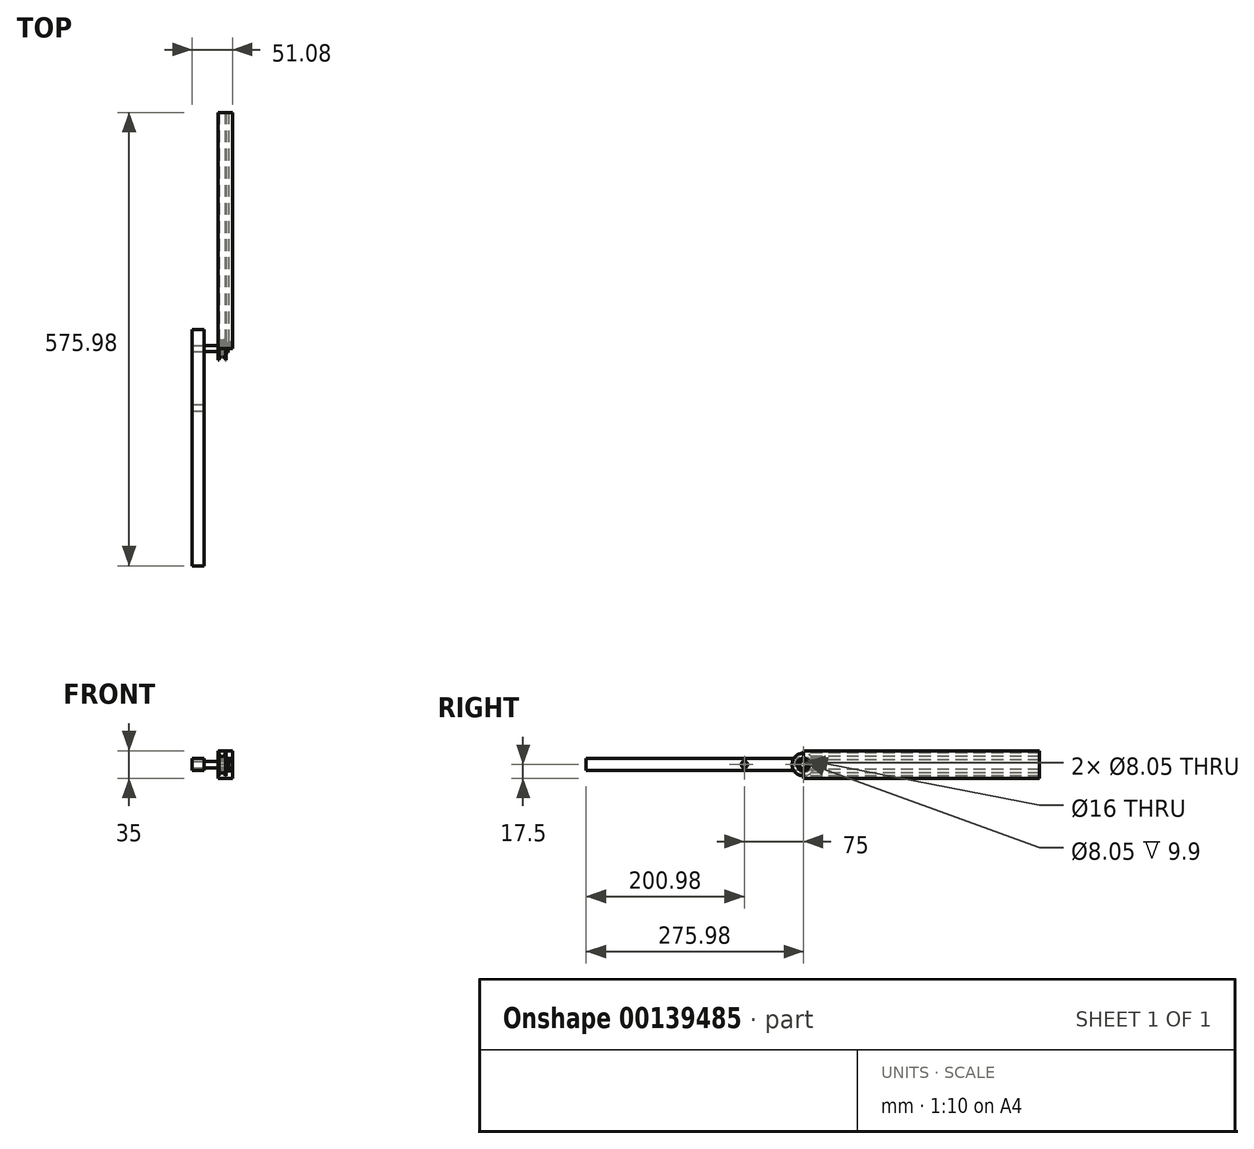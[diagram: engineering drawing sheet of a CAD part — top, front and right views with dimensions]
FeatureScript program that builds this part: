
annotation { "Feature Type Name" : "Feature", "Feature Type Description" : "" }
export const myFeature = defineFeature(function(context is Context, id is Id, definition is map)
    precondition{}
    {
        {
            var Q0;
            Q0=qCreatedBy(makeId("Front.planeOp"),FACE);
            var sketch = newSketch(context, id + "F0", { "sketchPlane" : qUnion([Q0])});
            skLineSegment(sketch, "E0.top", {"start": v(0, 35) * mm, "end": v(-13, 35) * mm});
            skLineSegment(sketch, "E1.0", {"start": v(-3, 32) * mm, "end": v(-13, 32) * mm});
            skLineSegment(sketch, "E1.1", {"start": v(-3, 23.5) * mm, "end": v(-3, 32) * mm});
            skLineSegment(sketch, "E2.trimOffspring", {"start": v(-13, 32) * mm, "end": v(-13, 35) * mm});
            skPoint(sketch, "E3", {"position": v(-4, 32) * mm});
            skPoint(sketch, "E4", {"position": v(-12, 32) * mm});
            skArc(sketch, "E5", {"start": v(-12, 32) * mm, "mid": v(-8, 28) * mm, "end": v(-4, 32) * mm});
            skPoint(sketch, "E0.bottom.start.orphan", {"position": v(0, 0) * mm});
            skPoint(sketch, "E6.MirrorP", {"position": v(-4, 3) * mm});
            skLineSegment(sketch, "E7.MirrorCS", {"start": v(0, 0) * mm, "end": v(-13, 0) * mm});
            skLineSegment(sketch, "E8.MirrorCS", {"start": v(-3, 3) * mm, "end": v(-13, 3) * mm});
            skLineSegment(sketch, "E9.MirrorCS", {"start": v(-3, 11.5) * mm, "end": v(-3, 3) * mm});
            skPoint(sketch, "E10.MirrorP", {"position": v(-12, 3) * mm});
            skArc(sketch, "E11.MirrorCS", {"start": v(-12, 3) * mm, "mid": v(-8, 7) * mm, "end": v(-4, 3) * mm});
            skLineSegment(sketch, "E12.MirrorCS", {"start": v(-13, 3) * mm, "end": v(-13, 0) * mm});
            skLineSegment(sketch, "E13", {"start": v(0, 35) * mm, "end": v(5, 35) * mm});
            skLineSegment(sketch, "E14", {"start": v(5, 35) * mm, "end": v(5, 0) * mm});
            skLineSegment(sketch, "E15", {"start": v(5, 0) * mm, "end": v(0, 0) * mm});
            skLineSegment(sketch, "E16", {"start": v(-3, 23.5) * mm, "end": v(0, 23.5) * mm});
            skLineSegment(sketch, "E17", {"start": v(0, 23.5) * mm, "end": v(0, 17.5) * mm});
            skLineSegment(sketch, "E18", {"start": v(0, 17.5) * mm, "end": v(5, 17.5) * mm, "construction": true});
            skLineSegment(sketch, "E19", {"start": v(0, 17.5) * mm, "end": v(0, 11.5) * mm});
            skLineSegment(sketch, "E20", {"start": v(0, 11.5) * mm, "end": v(-3, 11.5) * mm});
            skSolve(sketch);
        }
        {
            var Q0;
            Q0 = qSketchRegion(id + "F0", true);
            extrude(context, id + "F1", {"entities" : qUnion([Q0]), "oppositeDirection" : true, "depth" : 300 * mm});
        }
        {
            var Q0;
            Q0=qCreatedBy(makeId("Front.planeOp"),FACE);
            var sketch = newSketch(context, id + "F2", { "sketchPlane" : qUnion([Q0])});
            skArc(sketch, "E21.0", {"start": v(-12, 32) * mm, "mid": v(-8, 28) * mm, "end": v(-4, 32) * mm});
            skPoint(sketch, "E21.1", {"position": v(-13, 32) * mm});
            skLineSegment(sketch, "E21.2", {"start": v(-3, 32) * mm, "end": v(-4, 32) * mm});
            skLineSegment(sketch, "E21.3", {"start": v(-3, 23.5) * mm, "end": v(-3, 32) * mm});
            skLineSegment(sketch, "E21.4", {"start": v(-12, 3) * mm, "end": v(-13, 3) * mm});
            skArc(sketch, "E21.5", {"start": v(-12, 3) * mm, "mid": v(-8, 7) * mm, "end": v(-4, 3) * mm});
            skLineSegment(sketch, "E21.6", {"start": v(-3, 3) * mm, "end": v(-4, 3) * mm});
            skLineSegment(sketch, "E22.0", {"start": v(-12, 32) * mm, "end": v(-13, 32) * mm});
            skLineSegment(sketch, "E23.3", {"start": v(-12.1, 31.9) * mm, "end": v(-13, 31.9) * mm});
            skArc(sketch, "E23.4", {"start": v(-12.1, 31.9) * mm, "mid": v(-8, 27.9) * mm, "end": v(-3.9, 31.9) * mm});
            skLineSegment(sketch, "E23.5", {"start": v(-3.1, 31.9) * mm, "end": v(-3.9, 31.9) * mm});
            skLineSegment(sketch, "E23.6", {"start": v(-3.1, 17.5) * mm, "end": v(-3.1, 31.9) * mm});
            skLineSegment(sketch, "E24", {"start": v(-13, 31.9) * mm, "end": v(-13, 17.5) * mm});
            skLineSegment(sketch, "E25", {"start": v(-13, 17.5) * mm, "end": v(-3.1, 17.5) * mm});
            skSolve(sketch);
        }
        {
            var Q0;
            Q0 = qSketchRegion(id + "F2", true);
            var Q1;
            Q1=makeQuery(id+"F2.imprint","IMPRINT",FACE,{"disambiguationData":[TD([[makeQuery(id+"F2.imprint","IMPRINT",EDGE,{"derivedFrom":sQuery(id+"F2.wireOp",EDGE,"E23.3")}),1.0]])]});
            var Q2;
            Q2=sQuery(id+"F2.wireOp",EDGE,"E25");
            revolve(context, id + "F3", {"entities" : qUnion([Q0, Q1]), "axis" : qUnion([Q2]), "revolveType" : RevolveType.FULL});
        }
        {
            var Q0;
            Q0=makeQuery(id+"F3.opRevolve","SWEPT_FACE",FACE,{"disambiguationData":[OSD([sQuery(id+"F2.wireOp",EDGE,"E24")])]});
            var sketch = newSketch(context, id + "F4", { "sketchPlane" : qUnion([Q0])});
            skLineSegment(sketch, "E26", {"start": v(0, 3.1) * mm, "end": v(0, 31.9) * mm, "construction": true});
            skCircle(sketch, "E27", {"center": v(0, 17.5) * mm, "radius": 8 * mm});
            skCircle(sketch, "E28", {"center": v(0, 17.5) * mm, "radius": 4.03 * mm});
            skCircle(sketch, "E29", {"center": v(0, 17.5) * mm, "radius": 5 * mm});
            skCircle(sketch, "E30", {"center": v(0, 24) * mm, "radius": 1.5 * mm});
            skCircle(sketch, "E31.1.0", {"center": v(-3.82, 22.76) * mm, "radius": 1.5 * mm});
            skCircle(sketch, "E31.2.0", {"center": v(-6.18, 19.5) * mm, "radius": 1.5 * mm});
            skCircle(sketch, "E31.3.0", {"center": v(-6.18, 15.5) * mm, "radius": 1.5 * mm});
            skCircle(sketch, "E31.4.0", {"center": v(-3.82, 12.24) * mm, "radius": 1.5 * mm});
            skCircle(sketch, "E31.5.0", {"center": v(0, 11) * mm, "radius": 1.5 * mm});
            skCircle(sketch, "E31.6.0", {"center": v(3.82, 12.24) * mm, "radius": 1.5 * mm});
            skCircle(sketch, "E31.7.0", {"center": v(6.18, 15.5) * mm, "radius": 1.5 * mm});
            skCircle(sketch, "E31.8.0", {"center": v(6.18, 19.5) * mm, "radius": 1.5 * mm});
            skCircle(sketch, "E31.9.0", {"center": v(3.82, 22.76) * mm, "radius": 1.5 * mm});
            skSolve(sketch);
        }
        {
            var Q0;
            {var subQ0=sQuery(id+"F4.wireOp",EDGE,"E31.9.0");var subQ1=sQuery(id+"F4.wireOp",EDGE,"E27");var subQ2=makeQuery(id+"F4.imprint","INTERSECT",VERTEX,{"derivedFrom":[subQ1,subQ0]});Q0=makeQuery(id+"F4.imprint","IMPRINT",FACE,{"disambiguationData":[TD([[makeQuery(id+"F4.imprint","IMPRINT",EDGE,{"disambiguationData":[TD([[subQ2,-1.0]])],"derivedFrom":subQ1}),1.0]])]});}
            var Q1;
            {var subQ0=sQuery(id+"F4.wireOp",EDGE,"E31.9.0");var subQ1=sQuery(id+"F4.wireOp",EDGE,"E27");var subQ2=makeQuery(id+"F4.imprint","INTERSECT",VERTEX,{"derivedFrom":[subQ1,subQ0]});Q1=makeQuery(id+"F4.imprint","IMPRINT",FACE,{"disambiguationData":[TD([[makeQuery(id+"F4.imprint","IMPRINT",EDGE,{"disambiguationData":[TD([[subQ2,1.0]])],"derivedFrom":subQ1}),1.0]])]});}
            var Q2;
            {var subQ0=sQuery(id+"F4.wireOp",EDGE,"E31.8.0");var subQ1=sQuery(id+"F4.wireOp",EDGE,"E27");var subQ2=makeQuery(id+"F4.imprint","INTERSECT",VERTEX,{"derivedFrom":[subQ1,subQ0]});Q2=makeQuery(id+"F4.imprint","IMPRINT",FACE,{"disambiguationData":[TD([[makeQuery(id+"F4.imprint","IMPRINT",EDGE,{"disambiguationData":[TD([[subQ2,1.0]])],"derivedFrom":subQ1}),1.0]])]});}
            var Q3;
            {var subQ0=sQuery(id+"F4.wireOp",EDGE,"E30");var subQ1=sQuery(id+"F4.wireOp",EDGE,"E27");var subQ2=makeQuery(id+"F4.imprint","INTERSECT",VERTEX,{"derivedFrom":[subQ1,subQ0]});Q3=makeQuery(id+"F4.imprint","IMPRINT",FACE,{"disambiguationData":[TD([[makeQuery(id+"F4.imprint","IMPRINT",EDGE,{"disambiguationData":[TD([[subQ2,-1.0]])],"derivedFrom":subQ1}),1.0]])]});}
            var Q4;
            {var subQ0=sQuery(id+"F4.wireOp",EDGE,"E31.1.0");var subQ1=sQuery(id+"F4.wireOp",EDGE,"E27");var subQ2=makeQuery(id+"F4.imprint","INTERSECT",VERTEX,{"derivedFrom":[subQ1,subQ0]});Q4=makeQuery(id+"F4.imprint","IMPRINT",FACE,{"disambiguationData":[TD([[makeQuery(id+"F4.imprint","IMPRINT",EDGE,{"disambiguationData":[TD([[subQ2,-1.0]])],"derivedFrom":subQ1}),1.0]])]});}
            var Q5;
            {var subQ0=sQuery(id+"F4.wireOp",EDGE,"E31.2.0");var subQ1=sQuery(id+"F4.wireOp",EDGE,"E27");var subQ2=makeQuery(id+"F4.imprint","INTERSECT",VERTEX,{"derivedFrom":[subQ1,subQ0]});Q5=makeQuery(id+"F4.imprint","IMPRINT",FACE,{"disambiguationData":[TD([[makeQuery(id+"F4.imprint","IMPRINT",EDGE,{"disambiguationData":[TD([[subQ2,-1.0]])],"derivedFrom":subQ1}),1.0]])]});}
            var Q6;
            {var subQ0=sQuery(id+"F4.wireOp",EDGE,"E31.3.0");var subQ1=sQuery(id+"F4.wireOp",EDGE,"E27");var subQ2=makeQuery(id+"F4.imprint","INTERSECT",VERTEX,{"derivedFrom":[subQ1,subQ0]});Q6=makeQuery(id+"F4.imprint","IMPRINT",FACE,{"disambiguationData":[TD([[makeQuery(id+"F4.imprint","IMPRINT",EDGE,{"disambiguationData":[TD([[subQ2,-1.0]])],"derivedFrom":subQ1}),1.0]])]});}
            var Q7;
            {var subQ0=sQuery(id+"F4.wireOp",EDGE,"E31.4.0");var subQ1=sQuery(id+"F4.wireOp",EDGE,"E27");var subQ2=makeQuery(id+"F4.imprint","INTERSECT",VERTEX,{"derivedFrom":[subQ1,subQ0]});Q7=makeQuery(id+"F4.imprint","IMPRINT",FACE,{"disambiguationData":[TD([[makeQuery(id+"F4.imprint","IMPRINT",EDGE,{"disambiguationData":[TD([[subQ2,-1.0]])],"derivedFrom":subQ1}),1.0]])]});}
            var Q8;
            {var subQ0=sQuery(id+"F4.wireOp",EDGE,"E31.5.0");var subQ1=sQuery(id+"F4.wireOp",EDGE,"E27");var subQ2=makeQuery(id+"F4.imprint","INTERSECT",VERTEX,{"derivedFrom":[subQ1,subQ0]});Q8=makeQuery(id+"F4.imprint","IMPRINT",FACE,{"disambiguationData":[TD([[makeQuery(id+"F4.imprint","IMPRINT",EDGE,{"disambiguationData":[TD([[subQ2,-1.0]])],"derivedFrom":subQ1}),1.0]])]});}
            var Q9;
            {var subQ0=sQuery(id+"F4.wireOp",EDGE,"E31.6.0");var subQ1=sQuery(id+"F4.wireOp",EDGE,"E27");var subQ2=makeQuery(id+"F4.imprint","INTERSECT",VERTEX,{"derivedFrom":[subQ1,subQ0]});Q9=makeQuery(id+"F4.imprint","IMPRINT",FACE,{"disambiguationData":[TD([[makeQuery(id+"F4.imprint","IMPRINT",EDGE,{"disambiguationData":[TD([[subQ2,-1.0]])],"derivedFrom":subQ1}),1.0]])]});}
            var Q10;
            Q10=makeQuery(id+"F4.imprint","IMPRINT",FACE,{"disambiguationData":[TD([[makeQuery(id+"F4.imprint","IMPRINT",EDGE,{"derivedFrom":sQuery(id+"F4.wireOp",EDGE,"E28")}),1.0]])]});
            extrude(context, id + "F5", {"entities" : qUnion([Q0, Q1, Q2, Q3, Q4, Q5, Q6, Q7, Q8, Q9, Q10]), "operationType" : NewBodyOperationType.REMOVE, "endBound" : BoundingType.THROUGH_ALL, "oppositeDirection" : true, "depth" : 25 * mm});
        }
        {
            var Q0;
            Q0=qCreatedBy(makeId("Front.planeOp"),FACE);
            var sketch = newSketch(context, id + "F6", { "sketchPlane" : qUnion([Q0])});
            skLineSegment(sketch, "E32.0", {"start": v(-3, 17.5) * mm, "end": v(-3, 23.5) * mm});
            skLineSegment(sketch, "E32.1", {"start": v(-3.1, 21.5) * mm, "end": v(-3.1, 31.9) * mm});
            skLineSegment(sketch, "E32.2", {"start": v(-3, 32) * mm, "end": v(-4, 32) * mm});
            skLineSegment(sketch, "E32.3", {"start": v(-3.1, 31.9) * mm, "end": v(-3.9, 31.9) * mm});
            skArc(sketch, "E32.4", {"start": v(-12.1, 31.9) * mm, "mid": v(-8, 27.9) * mm, "end": v(-3.9, 31.9) * mm});
            skArc(sketch, "E32.5", {"start": v(-12, 32) * mm, "mid": v(-8, 28) * mm, "end": v(-4, 32) * mm});
            skLineSegment(sketch, "E32.6", {"start": v(-12.1, 31.9) * mm, "end": v(-13, 31.9) * mm});
            skLineSegment(sketch, "E32.7", {"start": v(-12, 32) * mm, "end": v(-13, 32) * mm});
            skLineSegment(sketch, "E32.8", {"start": v(-13, 32) * mm, "end": v(-13, 35) * mm});
            skLineSegment(sketch, "E32.9", {"start": v(0, 35) * mm, "end": v(-13, 35) * mm});
            skLineSegment(sketch, "E32.10", {"start": v(0, 35) * mm, "end": v(5, 35) * mm});
            skLineSegment(sketch, "E32.11", {"start": v(5, 35) * mm, "end": v(5, 0) * mm});
            skLineSegment(sketch, "E32.12", {"start": v(-3.1, 3.1) * mm, "end": v(-3.1, 17.5) * mm});
            skLineSegment(sketch, "E32.13", {"start": v(-13, 13.48) * mm, "end": v(-13, 17.5) * mm});
            skArc(sketch, "E32.15", {"start": v(-12, 3) * mm, "mid": v(-8, 7) * mm, "end": v(-4, 3) * mm});
            skLineSegment(sketch, "E32.16", {"start": v(-3, 3) * mm, "end": v(-4, 3) * mm});
            skLineSegment(sketch, "E32.19", {"start": v(-12, 3) * mm, "end": v(-13, 3) * mm});
            skLineSegment(sketch, "E33", {"start": v(-31.08, 17.5) * mm, "end": v(-3.1, 17.5) * mm});
            skPoint(sketch, "E33.startSnap0", {"position": v(-13, 17.5) * mm});
            skLineSegment(sketch, "E34", {"start": v(-3.1, 17.5) * mm, "end": v(-0.6, 17.5) * mm});
            skPoint(sketch, "E34.endSnap0", {"position": v(-3, 17.5) * mm});
            skLineSegment(sketch, "E35", {"start": v(-0.6, 17.5) * mm, "end": v(-0.6, 22.5) * mm});
            skLineSegment(sketch, "E36", {"start": v(-0.6, 22.5) * mm, "end": v(-3.1, 22.5) * mm});
            skLineSegment(sketch, "E37", {"start": v(-31.08, 21.5) * mm, "end": v(-3.1, 21.5) * mm});
            skLineSegment(sketch, "E38", {"start": v(-31.08, 21.5) * mm, "end": v(-31.08, 17.5) * mm});
            skLineSegment(sketch, "E39.trimOffspring", {"start": v(-3, 22.5) * mm, "end": v(-3, 32) * mm});
            skLineSegment(sketch, "E40.trimOffspring", {"start": v(-13, 21.5) * mm, "end": v(-13, 21.53) * mm});
            skSolve(sketch);
        }
        {
            var Q0;
            Q0 = qSketchRegion(id + "F6", true);
            var Q1;
            Q1=sQuery(id+"F6.wireOp",EDGE,"E33");
            revolve(context, id + "F7", {"entities" : qUnion([Q0]), "axis" : qUnion([Q1]), "revolveType" : RevolveType.FULL});
        }
        {
            var Q0;
            Q0=makeQuery(id+"F7.opRevolve","SWEPT_FACE",FACE,{"disambiguationData":[OSD([sQuery(id+"F6.wireOp",EDGE,"E38")])]});
            var sketch = newSketch(context, id + "F8", { "sketchPlane" : qUnion([Q0])});
            skLineSegment(sketch, "E41.bottom", {"start": v(-24.03, 25.03) * mm, "end": v(275.97, 25.03) * mm});
            skLineSegment(sketch, "E41.top", {"start": v(-24.03, 10.03) * mm, "end": v(275.97, 10.03) * mm});
            skLineSegment(sketch, "E41.left", {"start": v(-24.03, 25.03) * mm, "end": v(-24.03, 10.03) * mm});
            skLineSegment(sketch, "E41.right", {"start": v(275.97, 25.03) * mm, "end": v(275.97, 10.03) * mm});
            skPoint(sketch, "E42.0", {"position": v(0, 17.5) * mm});
            skCircle(sketch, "E42.1", {"center": v(0, 17.5) * mm, "radius": 4.03 * mm});
            skCircle(sketch, "E43", {"center": v(75, 17.5) * mm, "radius": 4.03 * mm});
            skSolve(sketch);
        }
        {
            var Q0;
            Q0 = qSketchRegion(id + "F8", true);
            extrude(context, id + "F9", {"entities" : qUnion([Q0]), "depth" : 15 * mm});
        }
    });
